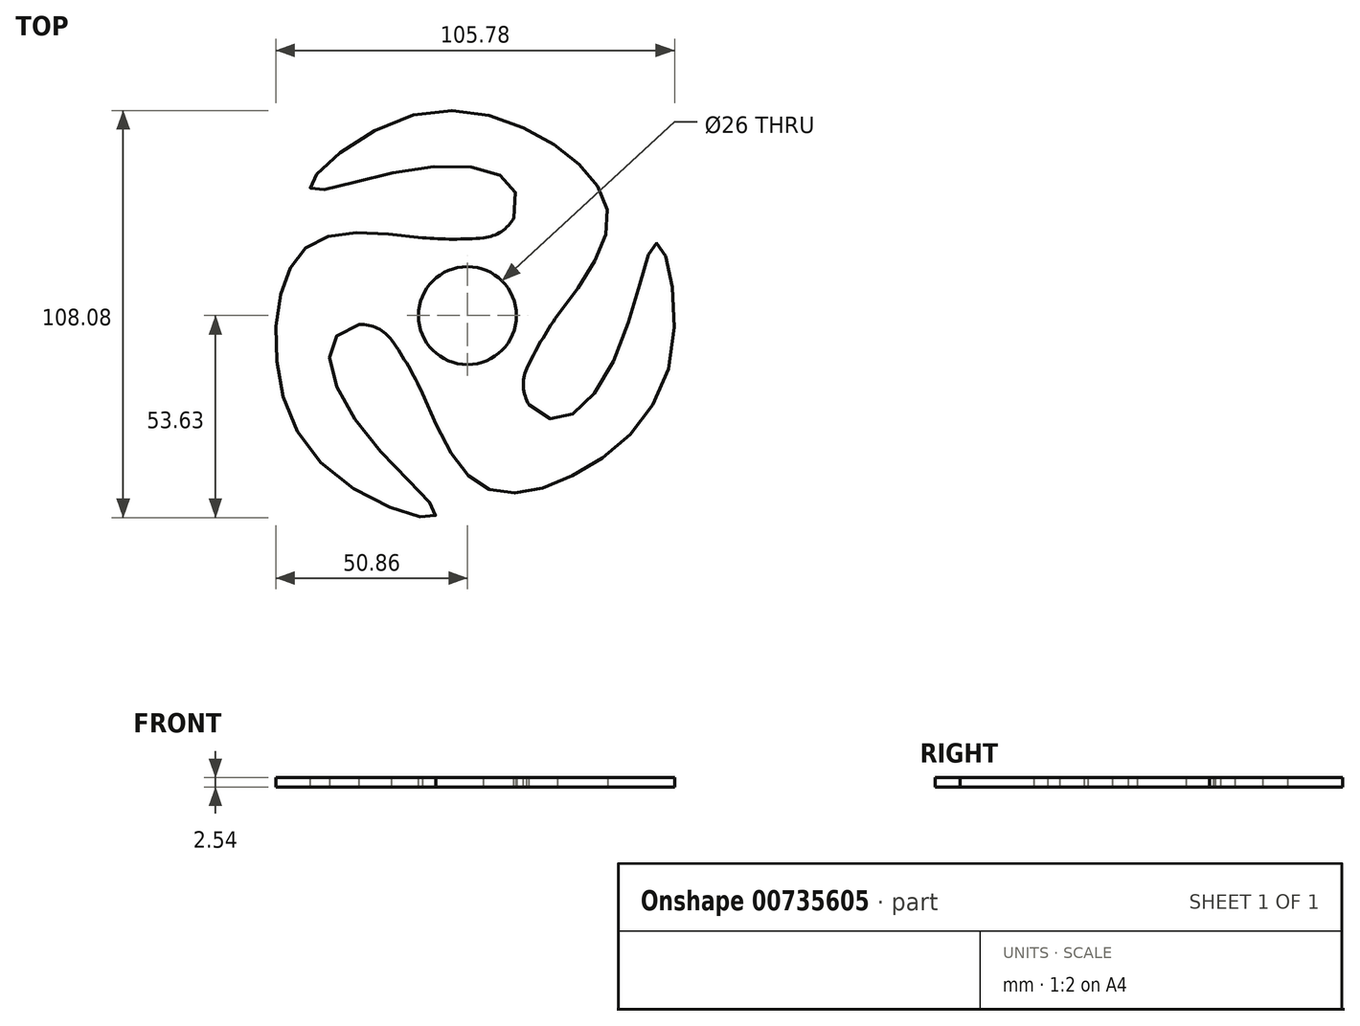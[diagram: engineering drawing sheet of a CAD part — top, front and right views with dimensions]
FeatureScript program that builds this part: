
annotation { "Feature Type Name" : "Feature", "Feature Type Description" : "" }
export const myFeature = defineFeature(function(context is Context, id is Id, definition is map)
    precondition{}
    {
        {
            var Q0;
            Q0=qCreatedBy(makeId("Top.planeOp"),FACE);
            var sketch = newSketch(context, id + "F0", { "sketchPlane" : qUnion([Q0])});
            skLineSegment(sketch, "E0", {"start": v(23.86, 0) * mm, "end": v(0, 0) * mm});
            skFitSpline(sketch, "E1", {"points": [v(23.86, 0) * mm, v(37.24, 25.73) * mm, v(23.86, 44.73) * mm, v(-16.28, 52.7) * mm, v(-41.75, 33.93) * mm, v(-13.26, 39.11) * mm, v(12.85, 32.2) * mm, v(0, 0) * mm, v(0, -17.64) * mm], "startDerivative": vector(160.43, 212.12) * mm, "endDerivative": vector(39.15, -159.06) * mm});
            skLineSegment(sketch, "E2.1.0", {"start": v(-11.93, 20.66) * mm, "end": v(0, 0) * mm});
            skLineSegment(sketch, "E2.2.0", {"start": v(-11.93, -20.66) * mm, "end": v(0, 0) * mm});
            skSolve(sketch);
        }
        {
            var Q0;
            Q0=makeQuery(id+"F0.imprint","IMPRINT",FACE,{"disambiguationData":[TD([[makeQuery(id+"F0.imprint","IMPRINT",EDGE,{"derivedFrom":sQuery(id+"F0.wireOp",EDGE,"E0")}),-1.0]])]});
            extrude(context, id + "F1", {"entities" : qUnion([Q0]), "endBound" : BoundingType.SYMMETRIC, "depth" : 2.54 * mm, "offsetDistance" : 25.4 * mm});
        }
        {
            var Q0;
            Q0=qCreatedBy(makeId("Front.planeOp"),FACE);
            var sketch = newSketch(context, id + "F2", { "sketchPlane" : qUnion([Q0])});
            skLineSegment(sketch, "E3", {"start": v(0, -22.17) * mm, "end": v(0, 33.63) * mm});
            skSolve(sketch);
        }
        {
            var Q0;
            Q0=makeQuery(id+"F1.opExtrude","SWEPT_BODY",BODY,{"disambiguationData":[OSD([sQuery(id+"F0.wireOp",EDGE,"E0"),sQuery(id+"F0.wireOp",EDGE,"E1")])]});
            var Q1;
            Q1=sQuery(id+"F2.wireOp",EDGE,"E3");
            circularPattern(context, id + "F3", {"entities" : qUnion([Q0]), "axis" : qUnion([Q1]), "angle" : 360 * degree, "instanceCount" : 3, "equalSpace" : true});
        }
        {
            var Q0;
            Q0=qCreatedBy(makeId("Top.planeOp"),FACE);
            var sketch = newSketch(context, id + "F4", { "sketchPlane" : qUnion([Q0])});
            skCircle(sketch, "E4", {"center": v(0, 0) * mm, "radius": 23.86 * mm});
            skSolve(sketch);
        }
        {
            var Q0;
            Q0=makeQuery(id+"F4.imprint","IMPRINT",FACE,{"disambiguationData":[TD([[makeQuery(id+"F4.imprint","IMPRINT",EDGE,{"derivedFrom":sQuery(id+"F4.wireOp",EDGE,"E4")}),1.0]])]});
            extrude(context, id + "F5", {"entities" : qUnion([Q0]), "endBound" : BoundingType.SYMMETRIC, "depth" : 2.54 * mm, "offsetDistance" : 25.4 * mm});
        }
        {
            var Q0;
            Q0=makeQuery(id+"F1.opExtrude","SWEPT_BODY",BODY,{"disambiguationData":[OSD([sQuery(id+"F0.wireOp",EDGE,"E0"),sQuery(id+"F0.wireOp",EDGE,"E1")])]});
            var Q1;
            Q1=makeQuery(id+"F3.opPattern","COPY",BODY,{"derivedFrom":makeQuery(id+"F1.opExtrude","SWEPT_BODY",BODY,{"disambiguationData":[OSD([sQuery(id+"F0.wireOp",EDGE,"E0"),sQuery(id+"F0.wireOp",EDGE,"E1")])]}),"instanceName":"1"});
            var Q2;
            Q2=makeQuery(id+"F5.opExtrude","SWEPT_BODY",BODY,{"disambiguationData":[OSD([sQuery(id+"F4.wireOp",EDGE,"E4")])]});
            var Q3;
            Q3=makeQuery(id+"F3.opPattern","COPY",BODY,{"derivedFrom":makeQuery(id+"F1.opExtrude","SWEPT_BODY",BODY,{"disambiguationData":[OSD([sQuery(id+"F0.wireOp",EDGE,"E0"),sQuery(id+"F0.wireOp",EDGE,"E1")])]}),"instanceName":"2"});
            booleanBodies(context, id + "F6", {"operationType" : BooleanOperationType.UNION, "tools" : qUnion([Q0, Q1, Q2, Q3])});
        }
        {
            var Q0;
            {var subQ0=makeQuery(id+"F1.opExtrude","CAP_FACE",FACE,{"disambiguationData":[OSD([sQuery(id+"F0.wireOp",EDGE,"E0"),sQuery(id+"F0.wireOp",EDGE,"E1")])],"isStart":false});Q0=makeQuery(id+"F6.opBoolean","MERGE",FACE,{"derivedFrom":[subQ0,makeQuery(id+"F3.opPattern","COPY",FACE,{"derivedFrom":subQ0,"instanceName":"1"}),makeQuery(id+"F3.opPattern","COPY",FACE,{"derivedFrom":subQ0,"instanceName":"2"}),makeQuery(id+"F5.opExtrude","CAP_FACE",FACE,{"disambiguationData":[OSD([sQuery(id+"F4.wireOp",EDGE,"E4")])],"isStart":false})]});}
            var sketch = newSketch(context, id + "F7", { "sketchPlane" : qUnion([Q0])});
            skArc(sketch, "E5", {"start": v(-11.93, 20.66) * mm, "mid": v(-0.65, 20.35) * mm, "end": v(10.6, 21.38) * mm});
            skLineSegment(sketch, "E6", {"start": v(-11.93, 20.66) * mm, "end": v(0, 35.46) * mm});
            skLineSegment(sketch, "E7", {"start": v(0, 35.46) * mm, "end": v(10.6, 21.38) * mm});
            skLineSegment(sketch, "E8.1.0", {"start": v(-30.7, -17.73) * mm, "end": v(-23.8, -1.52) * mm});
            skArc(sketch, "E8.1.1", {"start": v(-11.93, -20.66) * mm, "mid": v(-17.3, -10.74) * mm, "end": v(-23.8, -1.52) * mm});
            skLineSegment(sketch, "E8.1.2", {"start": v(-11.93, -20.66) * mm, "end": v(-30.7, -17.73) * mm});
            skLineSegment(sketch, "E8.2.0", {"start": v(30.7, -17.73) * mm, "end": v(13.22, -19.86) * mm});
            skArc(sketch, "E8.2.1", {"start": v(23.86, 0) * mm, "mid": v(17.95, -9.61) * mm, "end": v(13.22, -19.86) * mm});
            skLineSegment(sketch, "E8.2.2", {"start": v(23.86, 0) * mm, "end": v(30.7, -17.73) * mm});
            skPoint(sketch, "E8.center", {"position": v(0, 0) * mm});
            skSolve(sketch);
        }
        {
            var Q0;
            Q0=makeQuery(id+"F7.imprint","IMPRINT",FACE,{"disambiguationData":[TD([[makeQuery(id+"F7.imprint","IMPRINT",EDGE,{"derivedFrom":sQuery(id+"F7.wireOp",EDGE,"E5")}),1.0]])]});
            var Q1;
            Q1=makeQuery(id+"F7.imprint","IMPRINT",FACE,{"disambiguationData":[TD([[makeQuery(id+"F7.imprint","IMPRINT",EDGE,{"derivedFrom":sQuery(id+"F7.wireOp",EDGE,"E8.1.1")}),1.0]])]});
            var Q2;
            Q2=makeQuery(id+"F7.imprint","IMPRINT",FACE,{"disambiguationData":[TD([[makeQuery(id+"F7.imprint","IMPRINT",EDGE,{"derivedFrom":sQuery(id+"F7.wireOp",EDGE,"E8.2.1")}),1.0]])]});
            extrude(context, id + "F8", {"entities" : qUnion([Q0, Q1, Q2]), "operationType" : NewBodyOperationType.REMOVE, "oppositeDirection" : true, "depth" : 25.4 * mm, "offsetDistance" : 25.4 * mm});
        }
        {
            var Q0;
            {var subQ0=makeQuery(id+"F1.opExtrude","CAP_FACE",FACE,{"disambiguationData":[OSD([sQuery(id+"F0.wireOp",EDGE,"E0"),sQuery(id+"F0.wireOp",EDGE,"E1")])],"isStart":false});Q0=makeQuery(id+"F6.opBoolean","MERGE",FACE,{"derivedFrom":[subQ0,makeQuery(id+"F3.opPattern","COPY",FACE,{"derivedFrom":subQ0,"instanceName":"1"}),makeQuery(id+"F3.opPattern","COPY",FACE,{"derivedFrom":subQ0,"instanceName":"2"}),makeQuery(id+"F5.opExtrude","CAP_FACE",FACE,{"disambiguationData":[OSD([sQuery(id+"F4.wireOp",EDGE,"E4")])],"isStart":false})]});}
            var sketch = newSketch(context, id + "F9", { "sketchPlane" : qUnion([Q0])});
            skArc(sketch, "E9", {"start": v(4.33, 20.64) * mm, "mid": v(8.98, 22.33) * mm, "end": v(12.34, 25.98) * mm});
            skArc(sketch, "E10.1.0", {"start": v(-20.04, -6.57) * mm, "mid": v(-23.83, -3.38) * mm, "end": v(-28.67, -2.3) * mm});
            skArc(sketch, "E10.2.0", {"start": v(15.71, -14.07) * mm, "mid": v(14.85, -18.95) * mm, "end": v(16.34, -23.67) * mm});
            skPoint(sketch, "E10.center", {"position": v(0, 0) * mm});
            skSolve(sketch);
        }
        {
            var Q0;
            {var subQ0=sQuery(id+"F9.wireOp",EDGE,"E9");Q0=makeQuery(id+"F9.imprint","IMPRINT",FACE,{"disambiguationData":[TD([[makeQuery(id+"F9.imprint","IMPRINT",EDGE,{"derivedFrom":subQ0}),-1.0]])]});}
            var Q1;
            {var subQ0=sQuery(id+"F9.wireOp",EDGE,"E10.2.0");Q1=makeQuery(id+"F9.imprint","IMPRINT",FACE,{"disambiguationData":[TD([[makeQuery(id+"F9.imprint","IMPRINT",EDGE,{"derivedFrom":subQ0}),-1.0]])]});}
            var Q2;
            {var subQ0=sQuery(id+"F9.wireOp",EDGE,"E10.1.0");Q2=makeQuery(id+"F9.imprint","IMPRINT",FACE,{"disambiguationData":[TD([[makeQuery(id+"F9.imprint","IMPRINT",EDGE,{"derivedFrom":subQ0}),-1.0]])]});}
            extrude(context, id + "F10", {"entities" : qUnion([Q0, Q1, Q2]), "operationType" : NewBodyOperationType.ADD, "oppositeDirection" : true, "depth" : 2.54 * mm, "offsetDistance" : 25.4 * mm});
        }
        {
            var Q0;
            {var subQ0=sQuery(id+"F0.wireOp",EDGE,"E1");var subQ1=makeQuery(id+"F1.opExtrude","CAP_FACE",FACE,{"disambiguationData":[OSD([sQuery(id+"F0.wireOp",EDGE,"E0"),subQ0])],"isStart":false});Q0=makeQuery(id+"F10.boolean.opBoolean","MERGE",FACE,{"derivedFrom":[makeQuery(id+"F6.opBoolean","MERGE",FACE,{"derivedFrom":[subQ1,makeQuery(id+"F3.opPattern","COPY",FACE,{"derivedFrom":subQ1,"instanceName":"1"}),makeQuery(id+"F3.opPattern","COPY",FACE,{"derivedFrom":subQ1,"instanceName":"2"}),makeQuery(id+"F5.opExtrude","CAP_FACE",FACE,{"disambiguationData":[OSD([sQuery(id+"F4.wireOp",EDGE,"E4")])],"isStart":false})]}),makeQuery(id+"F10.opExtrude","CAP_FACE",FACE,{"disambiguationData":[OSD([subQ0,sQuery(id+"F7.wireOp",EDGE,"E5"),sQuery(id+"F9.wireOp",EDGE,"E9")])],"isStart":true}),makeQuery(id+"F10.opExtrude","CAP_FACE",FACE,{"disambiguationData":[OSD([subQ0,sQuery(id+"F7.wireOp",EDGE,"E8.1.1"),sQuery(id+"F9.wireOp",EDGE,"E10.1.0")])],"isStart":true}),makeQuery(id+"F10.opExtrude","CAP_FACE",FACE,{"disambiguationData":[OSD([subQ0,sQuery(id+"F7.wireOp",EDGE,"E8.2.1"),sQuery(id+"F9.wireOp",EDGE,"E10.2.0")])],"isStart":true})]});}
            var sketch = newSketch(context, id + "F11", { "sketchPlane" : qUnion([Q0])});
            skCircle(sketch, "E11", {"center": v(0, 0) * mm, "radius": 13 * mm});
            skSolve(sketch);
        }
        {
            var Q0;
            Q0=makeQuery(id+"F11.imprint","IMPRINT",FACE,{"disambiguationData":[TD([[makeQuery(id+"F11.imprint","IMPRINT",EDGE,{"derivedFrom":sQuery(id+"F11.wireOp",EDGE,"E11")}),1.0]])]});
            extrude(context, id + "F12", {"entities" : qUnion([Q0]), "operationType" : NewBodyOperationType.REMOVE, "oppositeDirection" : true, "depth" : 25.4 * mm, "offsetDistance" : 25.4 * mm});
        }
    });
